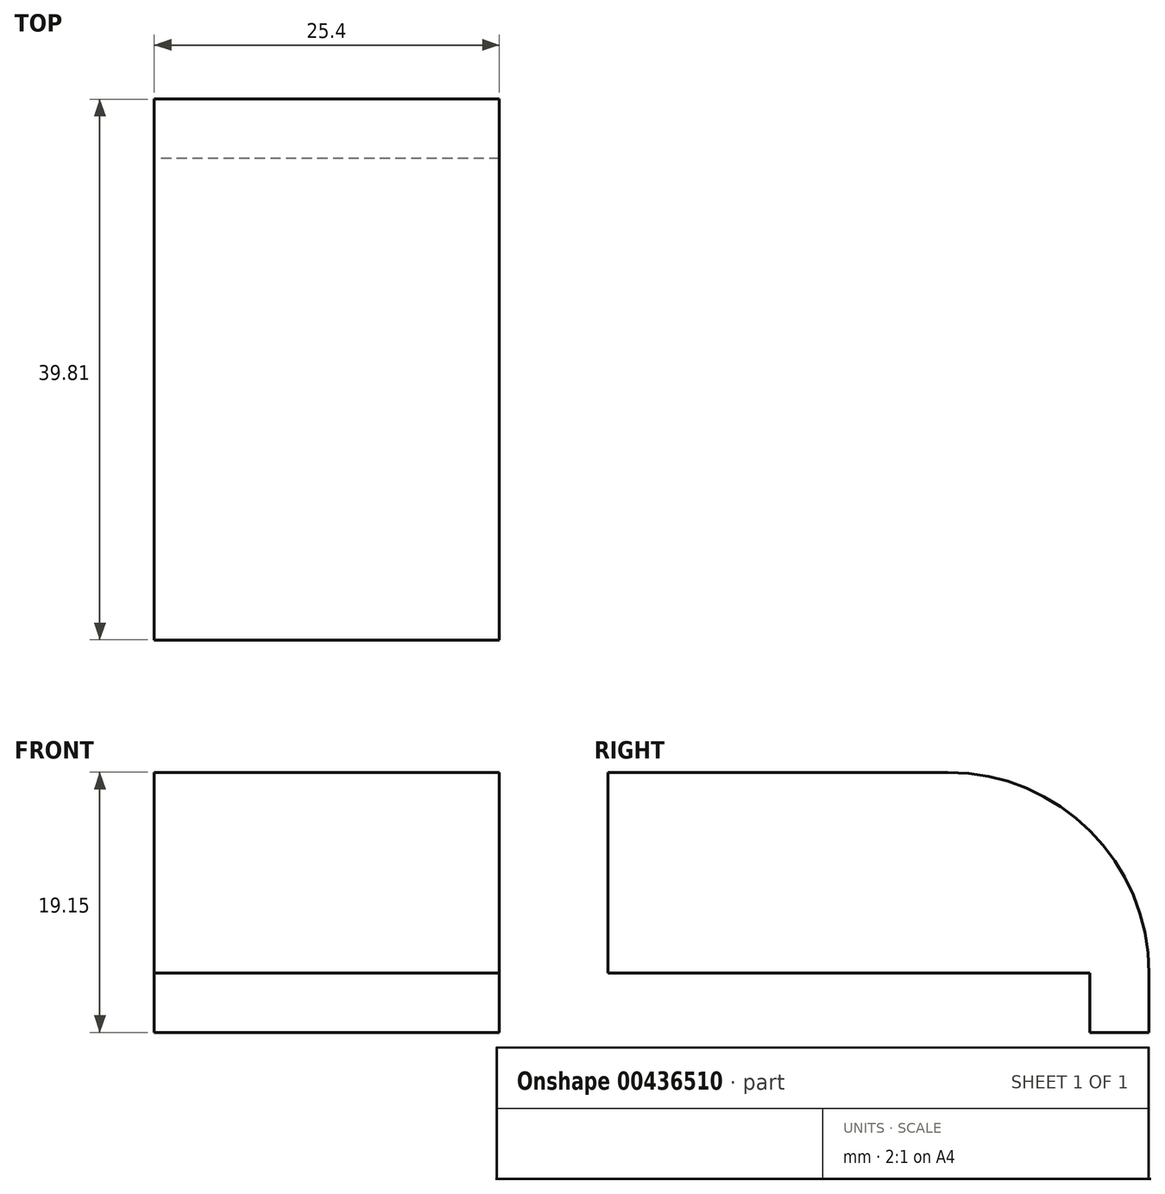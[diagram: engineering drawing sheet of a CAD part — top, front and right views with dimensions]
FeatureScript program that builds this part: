
annotation { "Feature Type Name" : "Feature", "Feature Type Description" : "" }
export const myFeature = defineFeature(function(context is Context, id is Id, definition is map)
    precondition{}
    {
        {
            var Q0;
            Q0=qCreatedBy(makeId("Right.planeOp"),FACE);
            var sketch = newSketch(context, id + "F0", { "sketchPlane" : qUnion([Q0])});
            skLineSegment(sketch, "E0.bottom", {"start": v(-44.93, 24.65) * mm, "end": v(-19.9, 24.65) * mm});
            skLineSegment(sketch, "E0.top", {"start": v(-44.93, 9.86) * mm, "end": v(-19.9, 9.86) * mm});
            skLineSegment(sketch, "E0.left", {"start": v(-44.93, 24.65) * mm, "end": v(-44.93, 9.86) * mm});
            skLineSegment(sketch, "E0.right", {"start": v(-19.9, 24.65) * mm, "end": v(-19.9, 9.86) * mm});
            skLineSegment(sketch, "E1.bottom", {"start": v(-35.45, 24.65) * mm, "end": v(-26.16, 24.65) * mm});
            skLineSegment(sketch, "E1.top", {"start": v(-35.45, 36.02) * mm, "end": v(-26.16, 36.02) * mm});
            skLineSegment(sketch, "E1.left", {"start": v(-35.45, 24.65) * mm, "end": v(-35.45, 36.02) * mm});
            skLineSegment(sketch, "E1.right", {"start": v(-26.16, 24.65) * mm, "end": v(-26.16, 36.02) * mm});
            skLineSegment(sketch, "E2.bottom", {"start": v(-19.9, 9.86) * mm, "end": v(-5.12, 9.86) * mm});
            skLineSegment(sketch, "E2.top", {"start": v(-19.9, -2.65) * mm, "end": v(-5.12, -2.65) * mm});
            skLineSegment(sketch, "E2.left", {"start": v(-19.9, 9.86) * mm, "end": v(-19.9, -2.65) * mm});
            skLineSegment(sketch, "E2.right", {"start": v(-5.12, 9.86) * mm, "end": v(-5.12, -2.65) * mm});
            skLineSegment(sketch, "E3.bottom", {"start": v(-9.48, 9.86) * mm, "end": v(-5.12, 9.86) * mm});
            skLineSegment(sketch, "E3.top", {"start": v(-9.48, 5.5) * mm, "end": v(-5.12, 5.5) * mm});
            skLineSegment(sketch, "E3.left", {"start": v(-9.48, 9.86) * mm, "end": v(-9.48, 5.5) * mm});
            skLineSegment(sketch, "E3.right", {"start": v(-5.12, 9.86) * mm, "end": v(-5.12, 5.5) * mm});
            skArc(sketch, "E4", {"start": v(-5.12, 9.86) * mm, "mid": v(-9.45, 20.32) * mm, "end": v(-19.9, 24.65) * mm});
            skSolve(sketch);
        }
        {
            var Q0;
            Q0=makeQuery(id+"F0.imprint","IMPRINT",FACE,{"disambiguationData":[TD([[makeQuery(id+"F0.imprint","IMPRINT",EDGE,{"derivedFrom":sQuery(id+"F0.wireOp",EDGE,"E0.top")}),1.0]])]});
            var Q1;
            Q1=makeQuery(id+"F0.imprint","IMPRINT",FACE,{"disambiguationData":[TD([[makeQuery(id+"F0.imprint","IMPRINT",EDGE,{"derivedFrom":sQuery(id+"F0.wireOp",EDGE,"E1.bottom")}),1.0]])]});
            var Q2;
            Q2=makeQuery(id+"F0.imprint","IMPRINT",FACE,{"disambiguationData":[TD([[makeQuery(id+"F0.imprint","IMPRINT",EDGE,{"derivedFrom":sQuery(id+"F0.wireOp",EDGE,"E2.bottom")}),-1.0]])]});
            var Q3;
            Q3=makeQuery(id+"F0.imprint","IMPRINT",FACE,{"disambiguationData":[TD([[makeQuery(id+"F0.imprint","IMPRINT",EDGE,{"derivedFrom":sQuery(id+"F0.wireOp",EDGE,"E0.right")}),1.0]])]});
            extrude(context, id + "F1", {"entities" : qUnion([Q0, Q1, Q2, Q3]), "depth" : 25.4 * mm});
        }
    });
